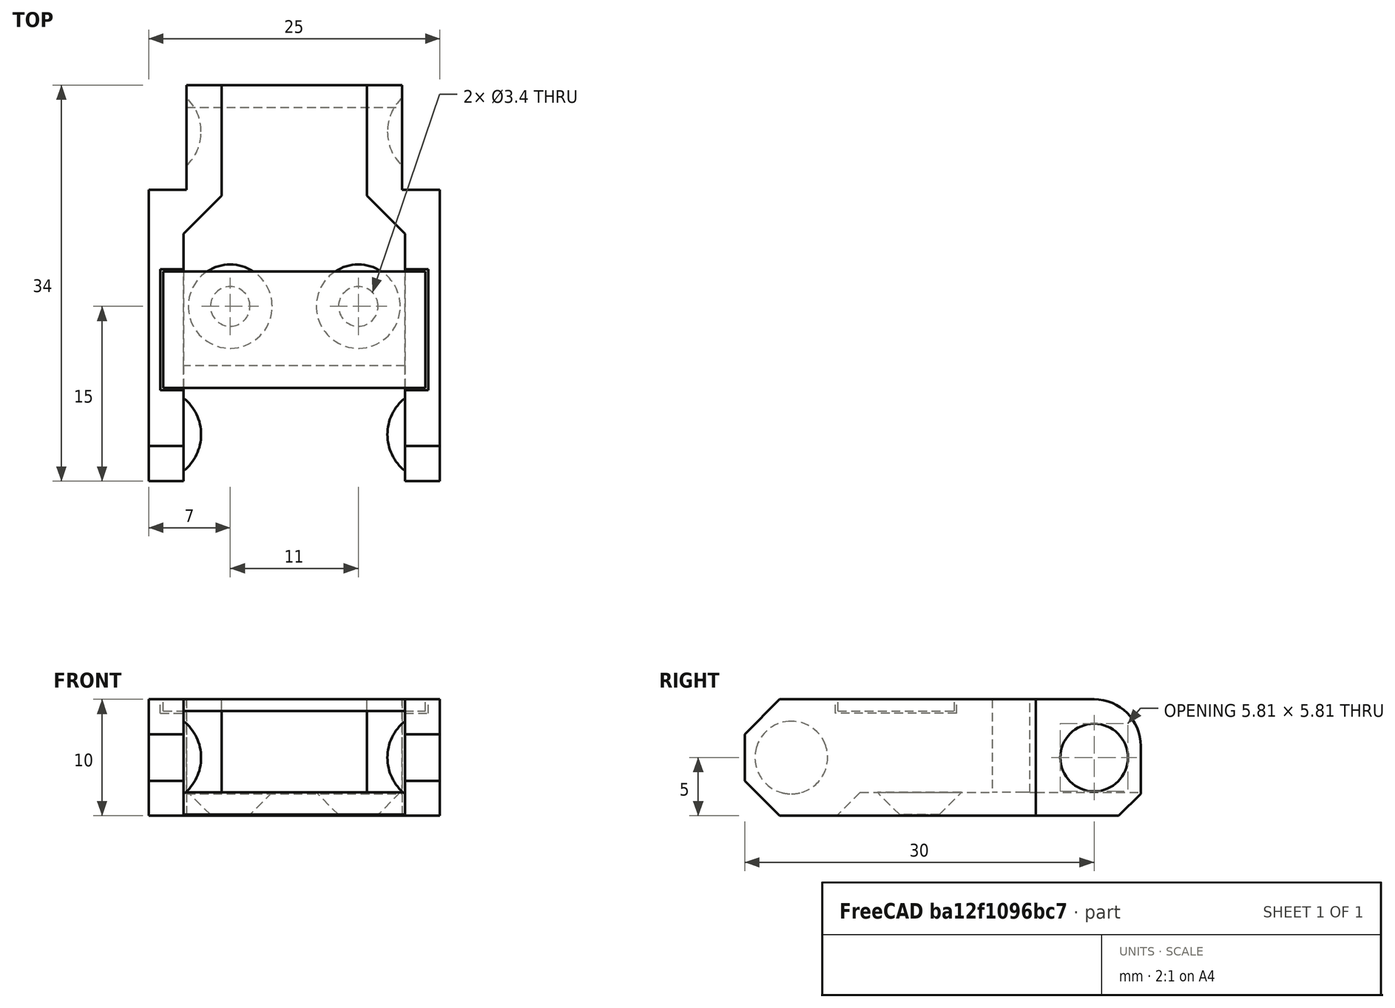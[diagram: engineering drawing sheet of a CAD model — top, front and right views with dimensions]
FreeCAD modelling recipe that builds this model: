
FCSTD DOCUMENT  (FreeCAD 0.18.4R)
Label: cable-chain
License: All rights reserved
LicenseURL: http://en.wikipedia.org/wiki/All_rights_reserved
objects: Part::Box×11, Part::Cut×8, Part::Chamfer×7, Part::Sphere×4, Part::MultiFuse×4, Part::Mirroring×3, Part::Cylinder×2, Part::Fillet×1
note: 40 computed .brp shape members not serialized (recipe doc carries the construction recipe); baked Part::Feature solids carry a one-line shape summary decoded from their .brp

FEATURE [Part::Box] Box  label="Cube"
  AttacherType = Attacher::AttachEngine3D
  Height = 10
  Length = 25
  Width = 25
FEATURE [Part::Box] Box001  label="Cube001"
  AttacherType = Attacher::AttachEngine3D
  Height = 10
  Length = 19
  Placement = pos=(3,-1,2) rot=(0,0,1;0rad)
  Width = 28
FEATURE [Part::Cut] Cut
  Base = -> Box
  Tool = -> Box001
FEATURE [Part::Box] Box002  label="Cube002"
  AttacherType = Attacher::AttachEngine3D
  Height = 10
  Length = 19
  Placement = pos=(3,0,-4) rot=(0,0,1;0rad)
  Width = 8
FEATURE [Part::Cut] Cut001
  Base = -> Cut
  Tool = -> Box002
FEATURE [Part::Sphere] Sphere
  Angle1 = -90
  Angle2 = 90
  Angle3 = 360
  AttacherType = Attacher::AttachEngine3D
  Placement = pos=(0,4,5) rot=(0,0,1;0rad)
  Radius = 4
FEATURE [Part::Box] Box003  label="Cube003"
  AttacherType = Attacher::AttachEngine3D
  Height = 10
  Length = 10
  Placement = pos=(-8,0,0) rot=(0,0,1;0rad)
  Width = 10
FEATURE [Part::Cut] Cut002
  Base = -> Sphere
  Placement = pos=(0.5,0,0) rot=(0,0,1;0rad)
  Tool = -> Box003
FEATURE [Part::Box] Box004  label="Cube004"
  AttacherType = Attacher::AttachEngine3D
  Height = 10
  Length = 10
  Placement = pos=(-8,0,0) rot=(0,0,1;0rad)
  Width = 10
FEATURE [Part::Sphere] Sphere001
  Angle1 = -90
  Angle2 = 90
  Angle3 = 360
  AttacherType = Attacher::AttachEngine3D
  Placement = pos=(0,4,5) rot=(0,0,1;0rad)
  Radius = 4
FEATURE [Part::Cut] Cut003
  Base = -> Sphere001
  Tool = -> Box004
FEATURE [Part::Mirroring] Part__Mirroring  label="Cut003 (Mirror #1)"
  Base = (12.5,0,0)
  Normal = (1,0,0)
  Placement = pos=(-0.5,0,0) rot=(0,0,1;0rad)
  Source = -> Cut003
FEATURE [Part::Box] Box005  label="Cube005"
  AttacherType = Attacher::AttachEngine3D
  Height = 10
  Length = 18.5
  Placement = pos=(3.25,24,0) rot=(0,0,1;0rad)
  Width = 10
FEATURE [Part::Sphere] Sphere002
  Angle1 = -90
  Angle2 = 90
  Angle3 = 360
  AttacherType = Attacher::AttachEngine3D
  Placement = pos=(0.5,4,5) rot=(0,0,1;0rad)
  Radius = 4
FEATURE [Part::Sphere] Sphere003
  Angle1 = -90
  Angle2 = 90
  Angle3 = 360
  AttacherType = Attacher::AttachEngine3D
  Placement = pos=(0.5,4,5) rot=(0,0,1;0rad)
  Radius = 4
FEATURE [Part::Mirroring] Part__Mirroring001  label="Sphere003 (Mirror #2)"
  Base = (12.5,0,0)
  Normal = (1,0,0)
  Source = -> Sphere003
FEATURE [Part::MultiFuse] Fusion001
  Placement = pos=(0,26,0) rot=(0,0,1;0rad)
  Shapes = -> [Sphere002,Part__Mirroring001]
FEATURE [Part::Box] Box006  label="Cube006"
  AttacherType = Attacher::AttachEngine3D
  Height = 10
  Length = 12.5
  Placement = pos=(6.25,23,2) rot=(0,0,1;0rad)
  Width = 12
FEATURE [Part::Cut] Cut004
  Base = -> Box005
  Tool = -> Box006
FEATURE [Part::Cut] Cut005
  Base = -> Cut004
  Tool = -> Fusion001
FEATURE [Part::Box] Box007  label="Cube007"
  AttacherType = Attacher::AttachEngine3D
  Height = 10
  Length = 6.25
  Placement = pos=(0,21,0) rot=(0,0,1;0rad)
  Width = 4
FEATURE [Part::Chamfer] Chamfer001
  Base = -> Box007
  Edges = 1 edges r=3.5: [Edge5]
FEATURE [Part::Chamfer] Chamfer002
  Base = -> Cut005
  Edges = 2 edges r=1: [Edge9,Edge11]
FEATURE [Part::Box] Box008  label="Cube008"
  AttacherType = Attacher::AttachEngine3D
  Height = 10
  Length = 6.25
  Placement = pos=(0,21,0) rot=(0,0,1;0rad)
  Width = 4
FEATURE [Part::Chamfer] Chamfer003
  Base = -> Box008
  Edges = 1 edges r=3.5: [Edge5]
FEATURE [Part::Mirroring] Part__Mirroring002  label="Chamfer003 (Mirror #3)"
  Base = (12.5,0,0)
  Normal = (1,0,0)
  Source = -> Chamfer003
FEATURE [Part::Box] Box010  label="Cube010"
  AttacherType = Attacher::AttachEngine3D
  Height = 2
  Length = 23
  Placement = pos=(1,7.8,8.8) rot=(0,0,1;0rad)
  Width = 10.4
FEATURE [Part::Box] Box011  label="lid"
  AttacherType = Attacher::AttachEngine3D
  Height = 1
  Length = 22.5
  Placement = pos=(1.25,8,9) rot=(0,0,1;0rad)
  Width = 10
FEATURE [Part::Cylinder] Cylinder
  Angle = 360
  AttacherType = Attacher::AttachEngine3D
  Height = 10
  Placement = pos=(7,12,-8) rot=(0,0,1;0rad)
  Radius = 1.7
FEATURE [Part::Cylinder] Cylinder001
  Angle = 360
  AttacherType = Attacher::AttachEngine3D
  Height = 10
  Placement = pos=(18,12,-8) rot=(0,0,1;0rad)
  Radius = 1.7
FEATURE [Part::MultiFuse] Fusion003
  Placement = pos=(0,3,2) rot=(0,0,1;0rad)
  Shapes = -> [Cylinder,Cylinder001]
FEATURE [Part::MultiFuse] Fusion
  Shapes = -> [Cut001,Part__Mirroring,Cut002]
FEATURE [Part::Chamfer] Chamfer
  Base = -> Fusion
  Edges = 4 edges r=3: [Edge8,Edge9,Edge19,Edge37]
FEATURE [Part::MultiFuse] Fusion004
  Shapes = -> [Chamfer001,Chamfer002,Part__Mirroring002,Chamfer]
FEATURE [Part::Cut] Cut006
  Base = -> Fusion004
  Tool = -> Box010
FEATURE [Part::Cut] Cut007
  Base = -> Cut006
  Tool = -> Fusion003
FEATURE [Part::Chamfer] Chamfer004  label="link-a"
  Base = -> Cut007
  Edges = 2 edges r=1.9: [Edge49,Edge50]
FEATURE [Part::Chamfer] Chamfer005
  Base = -> Chamfer004
  Edges = 1 edges r=1.9: [Edge3]
FEATURE [Part::Chamfer] Chamfer006  label="link-b"
  Base = -> Chamfer005
  Edges = 1 edges r=1.9: [Edge161]
FEATURE [Part::Fillet] Fillet  label="link"
  Base = -> Chamfer006
  Edges = 2 edges r=4: [Edge3,Edge6]
